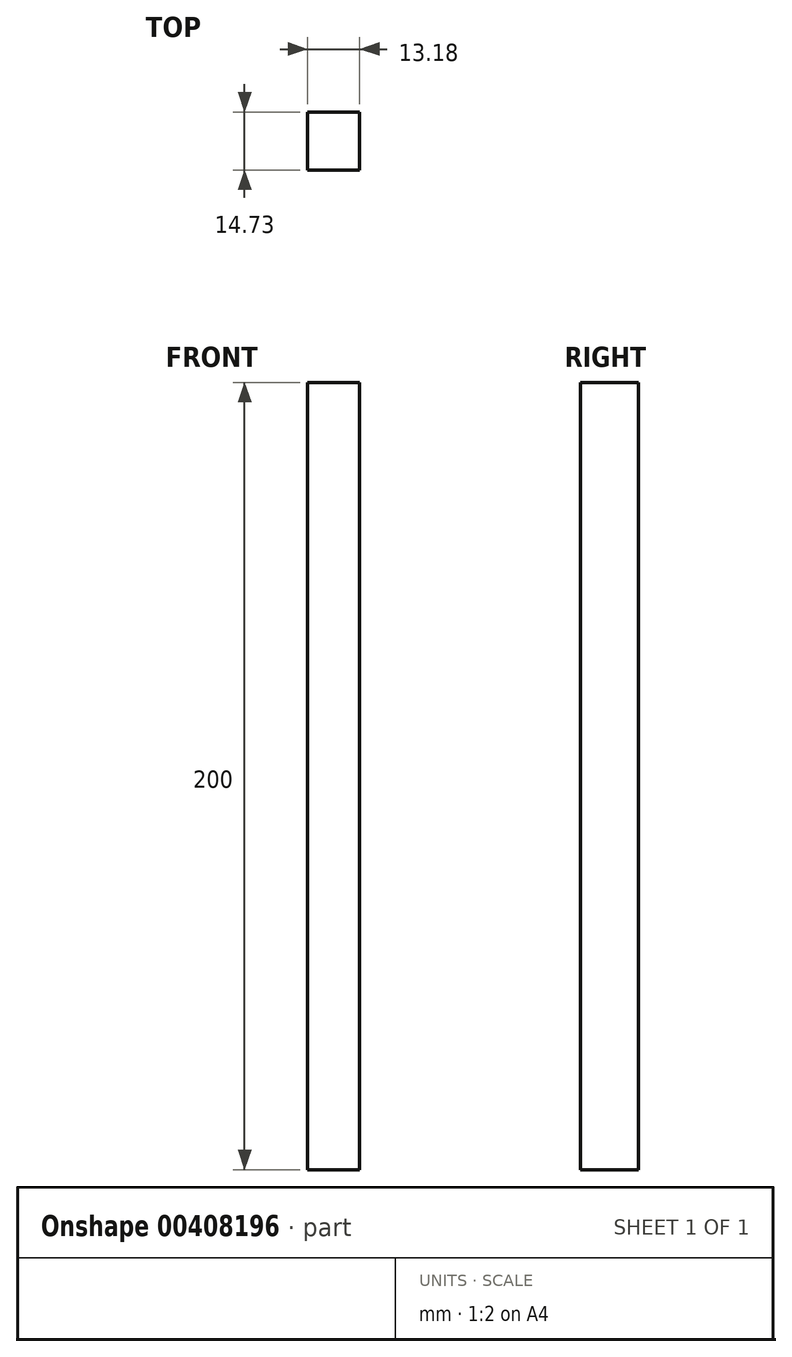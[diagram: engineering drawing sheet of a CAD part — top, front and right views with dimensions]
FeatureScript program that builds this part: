
annotation { "Feature Type Name" : "Feature", "Feature Type Description" : "" }
export const myFeature = defineFeature(function(context is Context, id is Id, definition is map)
    precondition{}
    {
        {
            var Q0;
            Q0=qCreatedBy(makeId("Top.planeOp"),FACE);
            var sketch = newSketch(context, id + "F0", { "sketchPlane" : qUnion([Q0])});
            skLineSegment(sketch, "E0.bottom", {"start": v(12.76, -27.56) * mm, "end": v(25.94, -27.56) * mm});
            skLineSegment(sketch, "E0.top", {"start": v(12.76, -42.3) * mm, "end": v(25.94, -42.3) * mm});
            skLineSegment(sketch, "E0.left", {"start": v(12.76, -27.56) * mm, "end": v(12.76, -42.3) * mm});
            skLineSegment(sketch, "E0.right", {"start": v(25.94, -27.56) * mm, "end": v(25.94, -42.3) * mm});
            skSolve(sketch);
        }
        {
            var Q0;
            Q0 = qSketchRegion(id + "F0", true);
            var Q1;
            Q1 = qConstructionFilter(qBodyType(qCreatedBy(id + "F0" ,EDGE), BodyType.WIRE), ConstructionObject.NO);
            extrude(context, id + "F1", {"entities" : qUnion([Q0]), "bodyType" : ToolBodyType.SURFACE, "surfaceEntities" : qUnion([Q1]), "depth" : 200 * mm});
        }
    });
